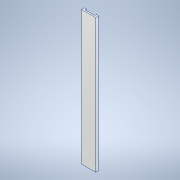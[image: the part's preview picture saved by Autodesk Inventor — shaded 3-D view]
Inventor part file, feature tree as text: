
AUTODESK INVENTOR PART (.ipt)
format: ipt  version: 2022 (Build 260153000, 153)  size: 103,936 bytes
history: native  units: mm
features: extrude x1, sketch x1
ambient origin geometry x8: Origin, YZ Plane, XZ Plane, XY Plane, X Axis, Y Axis, Z Axis, Center Point
bodies: Solid1 (feature_tree)
feature tree (2):
  extrude  "Extrusion1"  Depth=100.0mm
  sketch  "Sketch1"  dims[d0=20.0mm d1=100.0mm d2=950.0mm d3=0.0mm d4=10.0mm d5=16.0mm d6=16.0mm]
